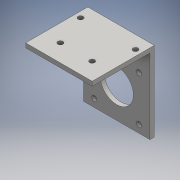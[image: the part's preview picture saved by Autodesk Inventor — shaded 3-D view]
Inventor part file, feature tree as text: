
AUTODESK INVENTOR PART (.ipt)
format: ipt  version: 2016 (Build 200138000, 138)  size: 187,904 bytes
history: native  units: mm
features: extrude x8, sketch x8, projected_geometry x4
ambient origin geometry x8: Origin, YZ Plane, XZ Plane, XY Plane, X Axis, Y Axis, Z Axis, Center Point
bodies: Body1 (feature_tree)
feature tree (20):
  extrude  "拉伸2"  Depth=42.0mm
  extrude  "拉伸3"  Depth=43.0mm
  extrude  "拉伸6"  Depth=3.0mm
  extrude  "拉伸8"  Depth=15.5mm
  extrude  "拉伸9"  Depth=15.5mm
  extrude  "拉伸10"  Depth=3.0mm TaperAngle=0.0deg
  extrude  "拉伸11"  Depth=9.0mm
  extrude  "拉伸12"  Depth=10.0mm
  sketch  "草图2"  dims[d3=42.0mm d4=42.0mm]
  sketch  "草图3"  dims[d5=3.0mm d6=0.0mm d7=43.0mm]
  sketch  "草图7"  dims[d8=3.0mm d9=0.0mm d17=23.0mm]
  sketch  "草图9"  dims[d18=3.5mm d19=15.5mm]
  sketch  "草图10"  dims[d20=15.5mm d21=15.5mm]
  projected_geometry  "投影回路1"
  sketch  "草图11"  dims[d22=15.5mm d23=3.0mm d24=0.0mm]
  projected_geometry  "投影回路2"
  sketch  "草图12"  dims[d32=3.5mm d34=9.0mm]
  projected_geometry  "投影回路3"
  sketch  "草图13"  dims[d35=19.0mm d36=3.5mm d37=11.0mm d38=22.0mm d39=10.0mm d40=0.0mm d41=2.0mm d42=0.0mm d43=2.0mm d44=0.0mm d45=10.0mm d46=0.0mm d47=10.0mm d48=0.0mm]
  projected_geometry  "投影回路4"
